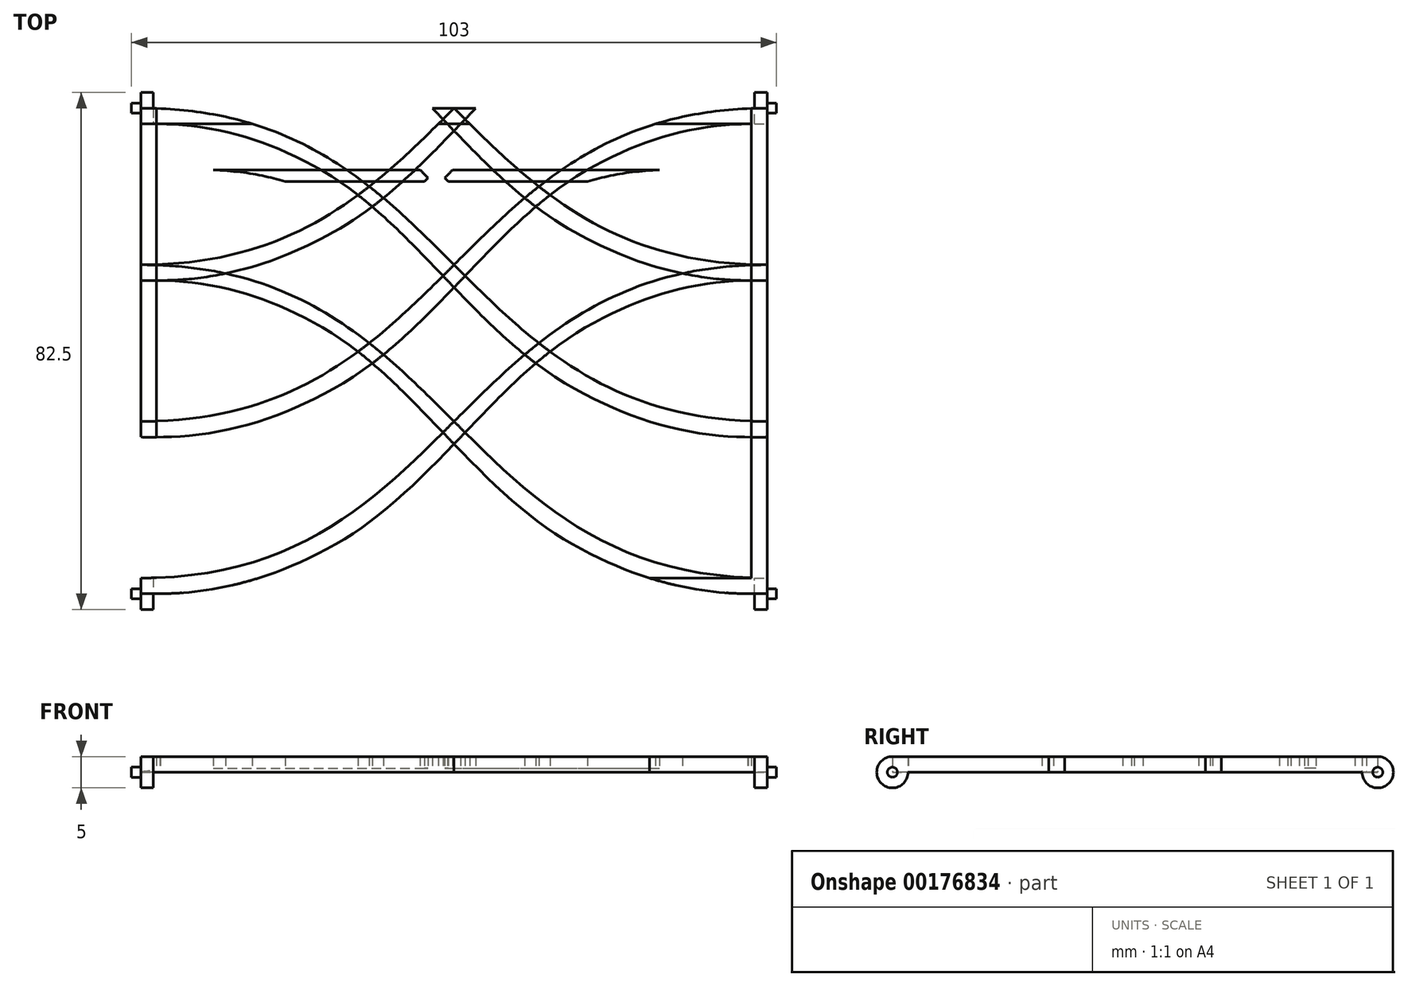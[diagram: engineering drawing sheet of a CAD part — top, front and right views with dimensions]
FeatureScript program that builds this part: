
annotation { "Feature Type Name" : "Feature", "Feature Type Description" : "" }
export const myFeature = defineFeature(function(context is Context, id is Id, definition is map)
    precondition{}
    {
        {
            var Q0;
            Q0=qCreatedBy(makeId("Top.planeOp"),FACE);
            var sketch = newSketch(context, id + "F0", { "sketchPlane" : qUnion([Q0])});
            skLineSegment(sketch, "E0.bottom", {"start": v(-50, 50) * mm, "end": v(50, 50) * mm});
            skLineSegment(sketch, "E0.top", {"start": v(-50, -50) * mm, "end": v(50, -50) * mm});
            skLineSegment(sketch, "E0.left", {"start": v(-50, 50) * mm, "end": v(-50, -50) * mm});
            skLineSegment(sketch, "E0.right", {"start": v(50, 50) * mm, "end": v(50, -50) * mm});
            skPoint(sketch, "E0.middle", {"position": v(0, 0) * mm});
            skLineSegment(sketch, "E1", {"start": v(-50, 50) * mm, "end": v(-50, 25) * mm});
            skLineSegment(sketch, "E2", {"start": v(-50, 25) * mm, "end": v(-50, 0) * mm});
            skLineSegment(sketch, "E3", {"start": v(-50, 0) * mm, "end": v(-50, -25) * mm});
            skLineSegment(sketch, "E4", {"start": v(-50, -25) * mm, "end": v(-50, -50) * mm});
            skFitSpline(sketch, "E5", {"points": [v(-50, 50) * mm, v(50, 0) * mm], "startDerivative": vector(150, 0) * mm, "endDerivative": vector(150, 0) * mm});
            skFitSpline(sketch, "E6", {"points": [v(-50, 25) * mm, v(50, -25) * mm], "startDerivative": vector(150, 0) * mm, "endDerivative": vector(150, 0) * mm});
            skFitSpline(sketch, "E7", {"points": [v(-50, 0) * mm, v(50, -50) * mm], "startDerivative": vector(150, 0) * mm, "endDerivative": vector(150, 0) * mm});
            skFitSpline(sketch, "E8", {"points": [v(-50, -50) * mm, v(50, 0) * mm], "startDerivative": vector(150, 0) * mm, "endDerivative": vector(150, 0) * mm});
            skFitSpline(sketch, "E9", {"points": [v(-50, -25) * mm, v(50, 25) * mm], "startDerivative": vector(150, 0) * mm, "endDerivative": vector(150, 0) * mm});
            skFitSpline(sketch, "E10", {"points": [v(-50, 0) * mm, v(50, 50) * mm], "startDerivative": vector(150, 0) * mm, "endDerivative": vector(150, 0) * mm});
            skFitSpline(sketch, "E11.0", {"points": [v(-50, 47.5) * mm, v(-46.98, 47.5) * mm, v(-41.34, 47.12) * mm, v(-33.93, 45.58) * mm, v(-27.38, 43.21) * mm, v(-19.56, 39.12) * mm, v(-11.07, 32.53) * mm, v(-1.8, 23.27) * mm, v(7.68, 13.78) * mm, v(16.77, 6.7) * mm, v(25.36, 2.2) * mm, v(32.58, -0.41) * mm, v(40.69, -2.1) * mm, v(46.77, -2.5) * mm, v(50, -2.5) * mm]});
            skFitSpline(sketch, "E12.0", {"points": [v(-50, -2.5) * mm, v(-46.77, -2.5) * mm, v(-40.69, -2.1) * mm, v(-32.58, -0.41) * mm, v(-25.36, 2.2) * mm, v(-16.77, 6.7) * mm, v(-7.68, 13.78) * mm, v(1.8, 23.27) * mm, v(11.07, 32.53) * mm, v(19.56, 39.12) * mm, v(27.38, 43.21) * mm, v(33.93, 45.58) * mm, v(41.34, 47.12) * mm, v(46.98, 47.5) * mm, v(50, 47.5) * mm]});
            skFitSpline(sketch, "E13.0", {"points": [v(-50, 22.5) * mm, v(-46.98, 22.5) * mm, v(-41.34, 22.12) * mm, v(-33.93, 20.58) * mm, v(-27.38, 18.21) * mm, v(-19.56, 14.12) * mm, v(-11.07, 7.53) * mm, v(-1.8, -1.73) * mm, v(7.68, -11.22) * mm, v(16.77, -18.3) * mm, v(25.36, -22.8) * mm, v(32.58, -25.41) * mm, v(40.69, -27.1) * mm, v(46.77, -27.5) * mm, v(50, -27.5) * mm]});
            skFitSpline(sketch, "E14.0", {"points": [v(-50, -27.5) * mm, v(-46.77, -27.5) * mm, v(-40.69, -27.1) * mm, v(-32.58, -25.41) * mm, v(-25.36, -22.8) * mm, v(-16.77, -18.3) * mm, v(-7.68, -11.22) * mm, v(1.8, -1.73) * mm, v(11.07, 7.53) * mm, v(19.56, 14.12) * mm, v(27.38, 18.21) * mm, v(33.93, 20.58) * mm, v(41.34, 22.12) * mm, v(46.98, 22.5) * mm, v(50, 22.5) * mm]});
            skFitSpline(sketch, "E15.0", {"points": [v(-50, -2.5) * mm, v(-46.98, -2.5) * mm, v(-41.34, -2.88) * mm, v(-33.93, -4.42) * mm, v(-27.38, -6.79) * mm, v(-19.56, -10.88) * mm, v(-11.07, -17.47) * mm, v(-1.8, -26.73) * mm, v(7.68, -36.22) * mm, v(16.77, -43.3) * mm, v(25.36, -47.8) * mm, v(32.58, -50.41) * mm, v(40.69, -52.1) * mm, v(46.77, -52.5) * mm, v(50, -52.5) * mm]});
            skFitSpline(sketch, "E16.0", {"points": [v(-50, -52.5) * mm, v(-46.77, -52.5) * mm, v(-40.69, -52.1) * mm, v(-32.58, -50.41) * mm, v(-25.36, -47.8) * mm, v(-16.77, -43.3) * mm, v(-7.68, -36.22) * mm, v(1.8, -26.73) * mm, v(11.07, -17.47) * mm, v(19.56, -10.88) * mm, v(27.38, -6.79) * mm, v(33.93, -4.42) * mm, v(41.34, -2.88) * mm, v(46.98, -2.5) * mm, v(50, -2.5) * mm]});
            skLineSegment(sketch, "E17", {"start": v(-50, -50) * mm, "end": v(-50, -52.5) * mm});
            skLineSegment(sketch, "E18", {"start": v(50, -52.5) * mm, "end": v(50, -50) * mm});
            skLineSegment(sketch, "E19", {"start": v(-50, 25) * mm, "end": v(50, 25) * mm});
            skLineSegment(sketch, "E20", {"start": v(-50, 25) * mm, "end": v(-47.5, 25) * mm});
            skLineSegment(sketch, "E21", {"start": v(50, 25) * mm, "end": v(47.5, 25) * mm});
            skLineSegment(sketch, "E22", {"start": v(-50, 22.5) * mm, "end": v(50, 22.5) * mm});
            skLineSegment(sketch, "E23", {"start": v(-47.5, 25) * mm, "end": v(-47.5, -49.96) * mm});
            skLineSegment(sketch, "E24", {"start": v(47.5, 25) * mm, "end": v(47.5, -50) * mm});
            skSolve(sketch);
        }
        {
            var Q0;
            {var subQ0=sQuery(id+"F0.wireOp",EDGE,"E23");var subQ9=sQuery(id+"F0.wireOp",EDGE,"E6");var subQ10=makeQuery(id+"F0.imprint","INTERSECT",VERTEX,{"derivedFrom":[subQ9,subQ0]});Q0=makeQuery(id+"F0.imprint","IMPRINT",FACE,{"disambiguationData":[TD([[makeQuery(id+"F0.imprint","IMPRINT",EDGE,{"disambiguationData":[TD([[subQ10,-1.0]])],"derivedFrom":subQ9}),1.0]])]});}
            var Q1;
            {var subQ0=sQuery(id+"F0.wireOp",EDGE,"E8");var subQ1=sQuery(id+"F0.wireOp",EDGE,"E7");var subQ2=makeQuery(id+"F0.imprint","INTERSECT",VERTEX,{"derivedFrom":[subQ1,subQ0]});Q1=makeQuery(id+"F0.imprint","IMPRINT",FACE,{"disambiguationData":[TD([[makeQuery(id+"F0.imprint","IMPRINT",EDGE,{"disambiguationData":[TD([[subQ2,-1.0]])],"derivedFrom":subQ1}),1.0]])]});}
            var Q2;
            {var subQ0=sQuery(id+"F0.wireOp",EDGE,"E16.0");var subQ1=sQuery(id+"F0.wireOp",EDGE,"E6");var subQ2=makeQuery(id+"F0.imprint","INTERSECT",VERTEX,{"derivedFrom":[subQ1,subQ0]});Q2=makeQuery(id+"F0.imprint","IMPRINT",FACE,{"disambiguationData":[TD([[makeQuery(id+"F0.imprint","IMPRINT",EDGE,{"disambiguationData":[TD([[subQ2,-1.0]])],"derivedFrom":subQ1}),-1.0]])]});}
            var Q3;
            {var subQ0=sQuery(id+"F0.wireOp",EDGE,"E9");var subQ1=sQuery(id+"F0.wireOp",EDGE,"E5");var subQ2=makeQuery(id+"F0.imprint","INTERSECT",VERTEX,{"derivedFrom":[subQ1,subQ0]});Q3=makeQuery(id+"F0.imprint","IMPRINT",FACE,{"disambiguationData":[TD([[makeQuery(id+"F0.imprint","IMPRINT",EDGE,{"disambiguationData":[TD([[subQ2,-1.0]])],"derivedFrom":subQ1}),-1.0]])]});}
            var Q4;
            {var subQ0=sQuery(id+"F0.wireOp",EDGE,"E9");var subQ1=sQuery(id+"F0.wireOp",EDGE,"E6");var subQ2=makeQuery(id+"F0.imprint","INTERSECT",VERTEX,{"derivedFrom":[subQ1,subQ0]});Q4=makeQuery(id+"F0.imprint","IMPRINT",FACE,{"disambiguationData":[TD([[makeQuery(id+"F0.imprint","IMPRINT",EDGE,{"disambiguationData":[TD([[subQ2,-1.0]])],"derivedFrom":subQ1}),1.0]])]});}
            var Q5;
            {var subQ1=sQuery(id+"F0.wireOp",EDGE,"E0.top");var subQ7=sQuery(id+"F0.wireOp",EDGE,"E24");var subQ9=makeQuery(id+"F0.imprint","INTERSECT",VERTEX,{"derivedFrom":[subQ1,subQ7]});Q5=makeQuery(id+"F0.imprint","IMPRINT",FACE,{"disambiguationData":[TD([[makeQuery(id+"F0.imprint","IMPRINT",EDGE,{"disambiguationData":[TD([[subQ9,1.0]])],"derivedFrom":subQ1}),1.0]])]});}
            var Q6;
            {var subQ0=sQuery(id+"F0.wireOp",EDGE,"E12.0");var subQ1=sQuery(id+"F0.wireOp",EDGE,"E6");var subQ2=makeQuery(id+"F0.imprint","INTERSECT",VERTEX,{"derivedFrom":[subQ1,subQ0]});Q6=makeQuery(id+"F0.imprint","IMPRINT",FACE,{"disambiguationData":[TD([[makeQuery(id+"F0.imprint","IMPRINT",EDGE,{"disambiguationData":[TD([[subQ2,-1.0]])],"derivedFrom":subQ1}),-1.0]])]});}
            var Q7;
            {var subQ0=sQuery(id+"F0.wireOp",EDGE,"E22");var subQ1=sQuery(id+"F0.wireOp",EDGE,"E6");var subQ2=makeQuery(id+"F0.imprint","INTERSECT",VERTEX,{"derivedFrom":[subQ1,subQ0]});Q7=makeQuery(id+"F0.imprint","IMPRINT",FACE,{"disambiguationData":[TD([[makeQuery(id+"F0.imprint","IMPRINT",EDGE,{"disambiguationData":[TD([[subQ2,-1.0]])],"derivedFrom":subQ1}),-1.0]])]});}
            var Q8;
            {var subQ0=sQuery(id+"F0.wireOp",EDGE,"E9");var subQ1=sQuery(id+"F0.wireOp",EDGE,"E7");var subQ2=makeQuery(id+"F0.imprint","INTERSECT",VERTEX,{"derivedFrom":[subQ1,subQ0]});Q8=makeQuery(id+"F0.imprint","IMPRINT",FACE,{"disambiguationData":[TD([[makeQuery(id+"F0.imprint","IMPRINT",EDGE,{"disambiguationData":[TD([[subQ2,-1.0]])],"derivedFrom":subQ1}),-1.0]])]});}
            var Q9;
            {var subQ1=sQuery(id+"F0.wireOp",EDGE,"E0.right");var subQ3=sQuery(id+"F0.wireOp",EDGE,"E13.0");var subQ4=makeQuery(id+"F0.imprint","INTERSECT",VERTEX,{"derivedFrom":[subQ1,subQ3]});Q9=makeQuery(id+"F0.imprint","IMPRINT",FACE,{"disambiguationData":[TD([[makeQuery(id+"F0.imprint","IMPRINT",EDGE,{"disambiguationData":[TD([[subQ4,1.0]])],"derivedFrom":subQ3}),-1.0]])]});}
            var Q10;
            {var subQ1=sQuery(id+"F0.wireOp",EDGE,"E8");var subQ5=makeQuery(id+"F0.imprint","INTERSECT",VERTEX,{"derivedFrom":[subQ1,sQuery(id+"F0.wireOp",EDGE,"E23")]});Q10=makeQuery(id+"F0.imprint","IMPRINT",FACE,{"disambiguationData":[TD([[makeQuery(id+"F0.imprint","IMPRINT",EDGE,{"disambiguationData":[TD([[subQ5,-1.0]])],"derivedFrom":subQ1}),-1.0]])]});}
            var Q11;
            {var subQ0=sQuery(id+"F0.wireOp",EDGE,"E6");var subQ1=sQuery(id+"F0.wireOp",EDGE,"E0.right");var subQ2=makeQuery(id+"F0.imprint","INTERSECT",VERTEX,{"derivedFrom":[subQ1,subQ0]});Q11=makeQuery(id+"F0.imprint","IMPRINT",FACE,{"disambiguationData":[TD([[makeQuery(id+"F0.imprint","IMPRINT",EDGE,{"disambiguationData":[TD([[subQ2,1.0]])],"derivedFrom":subQ0}),1.0]])]});}
            var Q12;
            {var subQ0=sQuery(id+"F0.wireOp",EDGE,"E5");var subQ5=sQuery(id+"F0.wireOp",EDGE,"E24");var subQ6=makeQuery(id+"F0.imprint","INTERSECT",VERTEX,{"derivedFrom":[subQ0,subQ5]});Q12=makeQuery(id+"F0.imprint","IMPRINT",FACE,{"disambiguationData":[TD([[makeQuery(id+"F0.imprint","IMPRINT",EDGE,{"disambiguationData":[TD([[subQ6,1.0]])],"derivedFrom":subQ5}),1.0]])]});}
            var Q13;
            {var subQ3=sQuery(id+"F0.wireOp",EDGE,"E12.0");var subQ5=sQuery(id+"F0.wireOp",EDGE,"E5");var subQ6=makeQuery(id+"F0.imprint","INTERSECT",VERTEX,{"derivedFrom":[subQ5,subQ3]});Q13=makeQuery(id+"F0.imprint","IMPRINT",FACE,{"disambiguationData":[TD([[makeQuery(id+"F0.imprint","IMPRINT",EDGE,{"disambiguationData":[TD([[subQ6,-1.0]])],"derivedFrom":subQ5}),1.0]])]});}
            var Q14;
            {var subQ1=sQuery(id+"F0.wireOp",EDGE,"E6");var subQ7=sQuery(id+"F0.wireOp",EDGE,"E10");var subQ8=makeQuery(id+"F0.imprint","INTERSECT",VERTEX,{"derivedFrom":[subQ1,subQ7]});Q14=makeQuery(id+"F0.imprint","IMPRINT",FACE,{"disambiguationData":[TD([[makeQuery(id+"F0.imprint","IMPRINT",EDGE,{"disambiguationData":[TD([[subQ8,-1.0]])],"derivedFrom":subQ1}),1.0]])]});}
            var Q15;
            {var subQ0=sQuery(id+"F0.wireOp",EDGE,"E10");var subQ5=sQuery(id+"F0.wireOp",EDGE,"E23");var subQ6=makeQuery(id+"F0.imprint","INTERSECT",VERTEX,{"derivedFrom":[subQ0,subQ5]});Q15=makeQuery(id+"F0.imprint","IMPRINT",FACE,{"disambiguationData":[TD([[makeQuery(id+"F0.imprint","IMPRINT",EDGE,{"disambiguationData":[TD([[subQ6,1.0]])],"derivedFrom":subQ5}),-1.0]])]});}
            var Q16;
            {var subQ0=sQuery(id+"F0.wireOp",EDGE,"E14.0");var subQ1=sQuery(id+"F0.wireOp",EDGE,"E5");var subQ2=makeQuery(id+"F0.imprint","INTERSECT",VERTEX,{"derivedFrom":[subQ1,subQ0]});Q16=makeQuery(id+"F0.imprint","IMPRINT",FACE,{"disambiguationData":[TD([[makeQuery(id+"F0.imprint","IMPRINT",EDGE,{"disambiguationData":[TD([[subQ2,-1.0]])],"derivedFrom":subQ1}),-1.0]])]});}
            var Q17;
            {var subQ4=sQuery(id+"F0.wireOp",EDGE,"E18");Q17=makeQuery(id+"F0.imprint","IMPRINT",FACE,{"disambiguationData":[TD([[makeQuery(id+"F0.imprint","IMPRINT",EDGE,{"derivedFrom":subQ4}),1.0]])]});}
            var Q18;
            {var subQ0=sQuery(id+"F0.wireOp",EDGE,"E23");var subQ1=sQuery(id+"F0.wireOp",EDGE,"E6");var subQ2=makeQuery(id+"F0.imprint","INTERSECT",VERTEX,{"derivedFrom":[subQ1,subQ0]});Q18=makeQuery(id+"F0.imprint","IMPRINT",FACE,{"disambiguationData":[TD([[makeQuery(id+"F0.imprint","IMPRINT",EDGE,{"disambiguationData":[TD([[subQ2,-1.0]])],"derivedFrom":subQ1}),-1.0]])]});}
            var Q19;
            {var subQ0=sQuery(id+"F0.wireOp",EDGE,"E8");var subQ1=sQuery(id+"F0.wireOp",EDGE,"E6");var subQ2=makeQuery(id+"F0.imprint","INTERSECT",VERTEX,{"derivedFrom":[subQ1,subQ0]});Q19=makeQuery(id+"F0.imprint","IMPRINT",FACE,{"disambiguationData":[TD([[makeQuery(id+"F0.imprint","IMPRINT",EDGE,{"disambiguationData":[TD([[subQ2,-1.0]])],"derivedFrom":subQ1}),-1.0]])]});}
            var Q20;
            {var subQ0=sQuery(id+"F0.wireOp",EDGE,"E17");Q20=makeQuery(id+"F0.imprint","IMPRINT",FACE,{"disambiguationData":[TD([[makeQuery(id+"F0.imprint","IMPRINT",EDGE,{"derivedFrom":subQ0}),1.0]])]});}
            var Q21;
            {var subQ0=sQuery(id+"F0.wireOp",EDGE,"E11.0");var subQ1=sQuery(id+"F0.wireOp",EDGE,"E8");var subQ2=makeQuery(id+"F0.imprint","INTERSECT",VERTEX,{"derivedFrom":[subQ1,subQ0]});Q21=makeQuery(id+"F0.imprint","IMPRINT",FACE,{"disambiguationData":[TD([[makeQuery(id+"F0.imprint","IMPRINT",EDGE,{"disambiguationData":[TD([[subQ2,-1.0]])],"derivedFrom":subQ1}),-1.0]])]});}
            var Q22;
            {var subQ0=sQuery(id+"F0.wireOp",EDGE,"E10");var subQ1=sQuery(id+"F0.wireOp",EDGE,"E6");var subQ2=makeQuery(id+"F0.imprint","INTERSECT",VERTEX,{"derivedFrom":[subQ1,subQ0]});Q22=makeQuery(id+"F0.imprint","IMPRINT",FACE,{"disambiguationData":[TD([[makeQuery(id+"F0.imprint","IMPRINT",EDGE,{"disambiguationData":[TD([[subQ2,-1.0]])],"derivedFrom":subQ1}),-1.0]])]});}
            var Q23;
            {var subQ1=sQuery(id+"F0.wireOp",EDGE,"E5");var subQ5=sQuery(id+"F0.wireOp",EDGE,"E9");var subQ6=makeQuery(id+"F0.imprint","INTERSECT",VERTEX,{"derivedFrom":[subQ1,subQ5]});Q23=makeQuery(id+"F0.imprint","IMPRINT",FACE,{"disambiguationData":[TD([[makeQuery(id+"F0.imprint","IMPRINT",EDGE,{"disambiguationData":[TD([[subQ6,-1.0]])],"derivedFrom":subQ1}),1.0]])]});}
            var Q24;
            {var subQ0=sQuery(id+"F0.wireOp",EDGE,"E9");var subQ1=sQuery(id+"F0.wireOp",EDGE,"E7");var subQ2=makeQuery(id+"F0.imprint","INTERSECT",VERTEX,{"derivedFrom":[subQ1,subQ0]});Q24=makeQuery(id+"F0.imprint","IMPRINT",FACE,{"disambiguationData":[TD([[makeQuery(id+"F0.imprint","IMPRINT",EDGE,{"disambiguationData":[TD([[subQ2,-1.0]])],"derivedFrom":subQ1}),1.0]])]});}
            var Q25;
            {var subQ1=sQuery(id+"F0.wireOp",EDGE,"E4");var subQ3=sQuery(id+"F0.wireOp",EDGE,"E14.0");var subQ4=makeQuery(id+"F0.imprint","INTERSECT",VERTEX,{"derivedFrom":[subQ1,subQ3]});Q25=makeQuery(id+"F0.imprint","IMPRINT",FACE,{"disambiguationData":[TD([[makeQuery(id+"F0.imprint","IMPRINT",EDGE,{"disambiguationData":[TD([[subQ4,-1.0]])],"derivedFrom":subQ3}),-1.0]])]});}
            var Q26;
            {var subQ5=sQuery(id+"F0.wireOp",EDGE,"E12.0");var subQ6=sQuery(id+"F0.wireOp",EDGE,"E7");var subQ7=makeQuery(id+"F0.imprint","INTERSECT",VERTEX,{"derivedFrom":[subQ6,subQ5]});Q26=makeQuery(id+"F0.imprint","IMPRINT",FACE,{"disambiguationData":[TD([[makeQuery(id+"F0.imprint","IMPRINT",EDGE,{"disambiguationData":[TD([[subQ7,-1.0]])],"derivedFrom":subQ6}),-1.0]])]});}
            var Q27;
            {var subQ0=sQuery(id+"F0.wireOp",EDGE,"E9");var subQ5=sQuery(id+"F0.wireOp",EDGE,"E23");var subQ6=makeQuery(id+"F0.imprint","INTERSECT",VERTEX,{"derivedFrom":[subQ0,subQ5]});Q27=makeQuery(id+"F0.imprint","IMPRINT",FACE,{"disambiguationData":[TD([[makeQuery(id+"F0.imprint","IMPRINT",EDGE,{"disambiguationData":[TD([[subQ6,1.0]])],"derivedFrom":subQ5}),-1.0]])]});}
            var Q28;
            {var subQ1=sQuery(id+"F0.wireOp",EDGE,"E8");var subQ6=sQuery(id+"F0.wireOp",EDGE,"E6");var subQ9=makeQuery(id+"F0.imprint","INTERSECT",VERTEX,{"derivedFrom":[subQ6,subQ1]});Q28=makeQuery(id+"F0.imprint","IMPRINT",FACE,{"disambiguationData":[TD([[makeQuery(id+"F0.imprint","IMPRINT",EDGE,{"disambiguationData":[TD([[subQ9,-1.0]])],"derivedFrom":subQ6}),1.0]])]});}
            var Q29;
            {var subQ0=sQuery(id+"F0.wireOp",EDGE,"E22");var subQ1=sQuery(id+"F0.wireOp",EDGE,"E9");var subQ2=makeQuery(id+"F0.imprint","INTERSECT",VERTEX,{"derivedFrom":[subQ1,subQ0]});Q29=makeQuery(id+"F0.imprint","IMPRINT",FACE,{"disambiguationData":[TD([[makeQuery(id+"F0.imprint","IMPRINT",EDGE,{"disambiguationData":[TD([[subQ2,-1.0]])],"derivedFrom":subQ1}),-1.0]])]});}
            var Q30;
            {var subQ0=sQuery(id+"F0.wireOp",EDGE,"E14.0");var subQ1=sQuery(id+"F0.wireOp",EDGE,"E6");var subQ2=makeQuery(id+"F0.imprint","INTERSECT",VERTEX,{"derivedFrom":[subQ1,subQ0]});Q30=makeQuery(id+"F0.imprint","IMPRINT",FACE,{"disambiguationData":[TD([[makeQuery(id+"F0.imprint","IMPRINT",EDGE,{"disambiguationData":[TD([[subQ2,-1.0]])],"derivedFrom":subQ1}),-1.0]])]});}
            var Q31;
            {var subQ3=sQuery(id+"F0.wireOp",EDGE,"E22");var subQ6=sQuery(id+"F0.wireOp",EDGE,"E5");var subQ9=makeQuery(id+"F0.imprint","INTERSECT",VERTEX,{"derivedFrom":[subQ6,subQ3]});Q31=makeQuery(id+"F0.imprint","IMPRINT",FACE,{"disambiguationData":[TD([[makeQuery(id+"F0.imprint","IMPRINT",EDGE,{"disambiguationData":[TD([[subQ9,-1.0]])],"derivedFrom":subQ6}),-1.0]])]});}
            var Q32;
            {var subQ0=sQuery(id+"F0.wireOp",EDGE,"E14.0");var subQ1=sQuery(id+"F0.wireOp",EDGE,"E7");var subQ2=makeQuery(id+"F0.imprint","INTERSECT",VERTEX,{"derivedFrom":[subQ1,subQ0]});Q32=makeQuery(id+"F0.imprint","IMPRINT",FACE,{"disambiguationData":[TD([[makeQuery(id+"F0.imprint","IMPRINT",EDGE,{"disambiguationData":[TD([[subQ2,-1.0]])],"derivedFrom":subQ1}),-1.0]])]});}
            var Q33;
            {var subQ0=sQuery(id+"F0.wireOp",EDGE,"E23");var subQ1=sQuery(id+"F0.wireOp",EDGE,"E7");var subQ2=makeQuery(id+"F0.imprint","INTERSECT",VERTEX,{"derivedFrom":[subQ1,subQ0]});Q33=makeQuery(id+"F0.imprint","IMPRINT",FACE,{"disambiguationData":[TD([[makeQuery(id+"F0.imprint","IMPRINT",EDGE,{"disambiguationData":[TD([[subQ2,-1.0]])],"derivedFrom":subQ1}),-1.0]])]});}
            var Q34;
            {var subQ0=sQuery(id+"F0.wireOp",EDGE,"E23");var subQ1=sQuery(id+"F0.wireOp",EDGE,"E9");var subQ2=makeQuery(id+"F0.imprint","INTERSECT",VERTEX,{"derivedFrom":[subQ1,subQ0]});Q34=makeQuery(id+"F0.imprint","IMPRINT",FACE,{"disambiguationData":[TD([[makeQuery(id+"F0.imprint","IMPRINT",EDGE,{"disambiguationData":[TD([[subQ2,-1.0]])],"derivedFrom":subQ1}),-1.0]])]});}
            var Q35;
            {var subQ5=sQuery(id+"F0.wireOp",EDGE,"E23");var subQ6=sQuery(id+"F0.wireOp",EDGE,"E7");var subQ7=makeQuery(id+"F0.imprint","INTERSECT",VERTEX,{"derivedFrom":[subQ6,subQ5]});Q35=makeQuery(id+"F0.imprint","IMPRINT",FACE,{"disambiguationData":[TD([[makeQuery(id+"F0.imprint","IMPRINT",EDGE,{"disambiguationData":[TD([[subQ7,-1.0]])],"derivedFrom":subQ6}),1.0]])]});}
            var Q36;
            {var subQ0=sQuery(id+"F0.wireOp",EDGE,"E12.0");var subQ1=sQuery(id+"F0.wireOp",EDGE,"E5");var subQ2=makeQuery(id+"F0.imprint","INTERSECT",VERTEX,{"derivedFrom":[subQ1,subQ0]});Q36=makeQuery(id+"F0.imprint","IMPRINT",FACE,{"disambiguationData":[TD([[makeQuery(id+"F0.imprint","IMPRINT",EDGE,{"disambiguationData":[TD([[subQ2,-1.0]])],"derivedFrom":subQ1}),-1.0]])]});}
            var Q37;
            {var subQ1=sQuery(id+"F0.wireOp",EDGE,"E7");var subQ3=sQuery(id+"F0.wireOp",EDGE,"E23");var subQ4=makeQuery(id+"F0.imprint","INTERSECT",VERTEX,{"derivedFrom":[subQ1,subQ3]});Q37=makeQuery(id+"F0.imprint","IMPRINT",FACE,{"disambiguationData":[TD([[makeQuery(id+"F0.imprint","IMPRINT",EDGE,{"disambiguationData":[TD([[subQ4,1.0]])],"derivedFrom":subQ3}),-1.0]])]});}
            var Q38;
            {var subQ0=sQuery(id+"F0.wireOp",EDGE,"E22");var subQ1=sQuery(id+"F0.wireOp",EDGE,"E10");var subQ2=makeQuery(id+"F0.imprint","INTERSECT",VERTEX,{"derivedFrom":[subQ1,subQ0]});Q38=makeQuery(id+"F0.imprint","IMPRINT",FACE,{"disambiguationData":[TD([[makeQuery(id+"F0.imprint","IMPRINT",EDGE,{"disambiguationData":[TD([[subQ2,-1.0]])],"derivedFrom":subQ1}),-1.0]])]});}
            var Q39;
            {var subQ0=sQuery(id+"F0.wireOp",EDGE,"E7");var subQ5=sQuery(id+"F0.wireOp",EDGE,"E23");var subQ6=makeQuery(id+"F0.imprint","INTERSECT",VERTEX,{"derivedFrom":[subQ0,subQ5]});Q39=makeQuery(id+"F0.imprint","IMPRINT",FACE,{"disambiguationData":[TD([[makeQuery(id+"F0.imprint","IMPRINT",EDGE,{"disambiguationData":[TD([[subQ6,-1.0]])],"derivedFrom":subQ5}),-1.0]])]});}
            var Q40;
            {var subQ0=sQuery(id+"F0.wireOp",EDGE,"E8");var subQ5=sQuery(id+"F0.wireOp",EDGE,"E24");var subQ6=makeQuery(id+"F0.imprint","INTERSECT",VERTEX,{"derivedFrom":[subQ0,subQ5]});Q40=makeQuery(id+"F0.imprint","IMPRINT",FACE,{"disambiguationData":[TD([[makeQuery(id+"F0.imprint","IMPRINT",EDGE,{"disambiguationData":[TD([[subQ6,-1.0]])],"derivedFrom":subQ5}),1.0]])]});}
            var Q41;
            {var subQ0=sQuery(id+"F0.wireOp",EDGE,"E6");var subQ1=sQuery(id+"F0.wireOp",EDGE,"E0.right");var subQ2=makeQuery(id+"F0.imprint","INTERSECT",VERTEX,{"derivedFrom":[subQ1,subQ0]});Q41=makeQuery(id+"F0.imprint","IMPRINT",FACE,{"disambiguationData":[TD([[makeQuery(id+"F0.imprint","IMPRINT",EDGE,{"disambiguationData":[TD([[subQ2,-1.0]])],"derivedFrom":subQ1}),-1.0]])]});}
            var Q42;
            {var subQ0=sQuery(id+"F0.wireOp",EDGE,"E22");var subQ1=sQuery(id+"F0.wireOp",EDGE,"E11.0");var subQ2=makeQuery(id+"F0.imprint","INTERSECT",VERTEX,{"derivedFrom":[subQ1,subQ0]});Q42=makeQuery(id+"F0.imprint","IMPRINT",FACE,{"disambiguationData":[TD([[makeQuery(id+"F0.imprint","IMPRINT",EDGE,{"disambiguationData":[TD([[subQ2,-1.0]])],"derivedFrom":subQ1}),1.0]])]});}
            var Q43;
            {var subQ1=sQuery(id+"F0.wireOp",EDGE,"E0.top");var subQ3=sQuery(id+"F0.wireOp",EDGE,"E24");var subQ4=makeQuery(id+"F0.imprint","INTERSECT",VERTEX,{"derivedFrom":[subQ1,subQ3]});Q43=makeQuery(id+"F0.imprint","IMPRINT",FACE,{"disambiguationData":[TD([[makeQuery(id+"F0.imprint","IMPRINT",EDGE,{"disambiguationData":[TD([[subQ4,1.0]])],"derivedFrom":subQ3}),1.0]])]});}
            var Q44;
            {var subQ1=sQuery(id+"F0.wireOp",EDGE,"E14.0");var subQ3=sQuery(id+"F0.wireOp",EDGE,"E24");var subQ4=makeQuery(id+"F0.imprint","INTERSECT",VERTEX,{"derivedFrom":[subQ1,subQ3]});Q44=makeQuery(id+"F0.imprint","IMPRINT",FACE,{"disambiguationData":[TD([[makeQuery(id+"F0.imprint","IMPRINT",EDGE,{"disambiguationData":[TD([[subQ4,1.0]])],"derivedFrom":subQ3}),1.0]])]});}
            var Q45;
            {var subQ0=sQuery(id+"F0.wireOp",EDGE,"E8");var subQ1=sQuery(id+"F0.wireOp",EDGE,"E7");var subQ2=makeQuery(id+"F0.imprint","INTERSECT",VERTEX,{"derivedFrom":[subQ1,subQ0]});Q45=makeQuery(id+"F0.imprint","IMPRINT",FACE,{"disambiguationData":[TD([[makeQuery(id+"F0.imprint","IMPRINT",EDGE,{"disambiguationData":[TD([[subQ2,-1.0]])],"derivedFrom":subQ1}),-1.0]])]});}
            var Q46;
            {var subQ0=sQuery(id+"F0.wireOp",EDGE,"E9");var subQ1=sQuery(id+"F0.wireOp",EDGE,"E6");var subQ2=makeQuery(id+"F0.imprint","INTERSECT",VERTEX,{"derivedFrom":[subQ1,subQ0]});Q46=makeQuery(id+"F0.imprint","IMPRINT",FACE,{"disambiguationData":[TD([[makeQuery(id+"F0.imprint","IMPRINT",EDGE,{"disambiguationData":[TD([[subQ2,-1.0]])],"derivedFrom":subQ1}),-1.0]])]});}
            var Q47;
            {var subQ1=sQuery(id+"F0.wireOp",EDGE,"E11.0");var subQ3=sQuery(id+"F0.wireOp",EDGE,"E24");var subQ4=makeQuery(id+"F0.imprint","INTERSECT",VERTEX,{"derivedFrom":[subQ1,subQ3]});Q47=makeQuery(id+"F0.imprint","IMPRINT",FACE,{"disambiguationData":[TD([[makeQuery(id+"F0.imprint","IMPRINT",EDGE,{"disambiguationData":[TD([[subQ4,-1.0]])],"derivedFrom":subQ3}),1.0]])]});}
            var Q48;
            {var subQ0=sQuery(id+"F0.wireOp",EDGE,"E11.0");var subQ1=sQuery(id+"F0.wireOp",EDGE,"E10");var subQ2=makeQuery(id+"F0.imprint","INTERSECT",VERTEX,{"derivedFrom":[subQ1,subQ0]});Q48=makeQuery(id+"F0.imprint","IMPRINT",FACE,{"disambiguationData":[TD([[makeQuery(id+"F0.imprint","IMPRINT",EDGE,{"disambiguationData":[TD([[subQ2,-1.0]])],"derivedFrom":subQ0}),1.0]])]});}
            var Q49;
            {var subQ1=sQuery(id+"F0.wireOp",EDGE,"E13.0");var subQ3=sQuery(id+"F0.wireOp",EDGE,"E23");var subQ4=makeQuery(id+"F0.imprint","INTERSECT",VERTEX,{"derivedFrom":[subQ1,subQ3]});Q49=makeQuery(id+"F0.imprint","IMPRINT",FACE,{"disambiguationData":[TD([[makeQuery(id+"F0.imprint","IMPRINT",EDGE,{"disambiguationData":[TD([[subQ4,1.0]])],"derivedFrom":subQ3}),-1.0]])]});}
            var Q50;
            {var subQ1=sQuery(id+"F0.wireOp",EDGE,"E4");var subQ3=sQuery(id+"F0.wireOp",EDGE,"E14.0");var subQ4=makeQuery(id+"F0.imprint","INTERSECT",VERTEX,{"derivedFrom":[subQ1,subQ3]});Q50=makeQuery(id+"F0.imprint","IMPRINT",FACE,{"disambiguationData":[TD([[makeQuery(id+"F0.imprint","IMPRINT",EDGE,{"disambiguationData":[TD([[subQ4,-1.0]])],"derivedFrom":subQ3}),1.0]])]});}
            var Q51;
            {var subQ1=sQuery(id+"F0.wireOp",EDGE,"E5");var subQ3=sQuery(id+"F0.wireOp",EDGE,"E24");var subQ4=makeQuery(id+"F0.imprint","INTERSECT",VERTEX,{"derivedFrom":[subQ1,subQ3]});Q51=makeQuery(id+"F0.imprint","IMPRINT",FACE,{"disambiguationData":[TD([[makeQuery(id+"F0.imprint","IMPRINT",EDGE,{"disambiguationData":[TD([[subQ4,-1.0]])],"derivedFrom":subQ3}),1.0]])]});}
            var Q52;
            {var subQ0=sQuery(id+"F0.wireOp",EDGE,"E11.0");var subQ1=sQuery(id+"F0.wireOp",EDGE,"E10");var subQ2=makeQuery(id+"F0.imprint","INTERSECT",VERTEX,{"derivedFrom":[subQ1,subQ0]});Q52=makeQuery(id+"F0.imprint","IMPRINT",FACE,{"disambiguationData":[TD([[makeQuery(id+"F0.imprint","IMPRINT",EDGE,{"disambiguationData":[TD([[subQ2,1.0]])],"derivedFrom":subQ0}),1.0]])]});}
            var Q53;
            {var subQ0=sQuery(id+"F0.wireOp",EDGE,"E6");var subQ5=sQuery(id+"F0.wireOp",EDGE,"E23");var subQ6=makeQuery(id+"F0.imprint","INTERSECT",VERTEX,{"derivedFrom":[subQ0,subQ5]});Q53=makeQuery(id+"F0.imprint","IMPRINT",FACE,{"disambiguationData":[TD([[makeQuery(id+"F0.imprint","IMPRINT",EDGE,{"disambiguationData":[TD([[subQ6,-1.0]])],"derivedFrom":subQ5}),-1.0]])]});}
            var Q54;
            {var subQ0=sQuery(id+"F0.wireOp",EDGE,"E9");var subQ5=sQuery(id+"F0.wireOp",EDGE,"E24");var subQ6=makeQuery(id+"F0.imprint","INTERSECT",VERTEX,{"derivedFrom":[subQ0,subQ5]});Q54=makeQuery(id+"F0.imprint","IMPRINT",FACE,{"disambiguationData":[TD([[makeQuery(id+"F0.imprint","IMPRINT",EDGE,{"disambiguationData":[TD([[subQ6,-1.0]])],"derivedFrom":subQ5}),1.0]])]});}
            var Q55;
            {var subQ0=sQuery(id+"F0.wireOp",EDGE,"E12.0");var subQ1=sQuery(id+"F0.wireOp",EDGE,"E5");var subQ2=makeQuery(id+"F0.imprint","INTERSECT",VERTEX,{"derivedFrom":[subQ1,subQ0]});Q55=makeQuery(id+"F0.imprint","IMPRINT",FACE,{"disambiguationData":[TD([[makeQuery(id+"F0.imprint","IMPRINT",EDGE,{"disambiguationData":[TD([[subQ2,-1.0]])],"derivedFrom":subQ0}),1.0]])]});}
            var Q56;
            {var subQ1=sQuery(id+"F0.wireOp",EDGE,"E12.0");var subQ3=sQuery(id+"F0.wireOp",EDGE,"E23");var subQ4=makeQuery(id+"F0.imprint","INTERSECT",VERTEX,{"derivedFrom":[subQ1,subQ3]});Q56=makeQuery(id+"F0.imprint","IMPRINT",FACE,{"disambiguationData":[TD([[makeQuery(id+"F0.imprint","IMPRINT",EDGE,{"disambiguationData":[TD([[subQ4,-1.0]])],"derivedFrom":subQ3}),-1.0]])]});}
            extrude(context, id + "F1", {"entities" : qUnion([Q0, Q1, Q2, Q3, Q4, Q5, Q6, Q7, Q8, Q9, Q10, Q11, Q12, Q13, Q14, Q15, Q16, Q17, Q18, Q19, Q20, Q21, Q22, Q23, Q24, Q25, Q26, Q27, Q28, Q29, Q30, Q31, Q32, Q33, Q34, Q35, Q36, Q37, Q38, Q39, Q40, Q41, Q42, Q43, Q44, Q45, Q46, Q47, Q48, Q49, Q50, Q51, Q52, Q53, Q54, Q55, Q56]), "depth" : 2.5 * mm});
        }
        {
            var Q0;
            Q0=makeQuery(id+"F1.opExtrude","SWEPT_FACE",FACE,{"disambiguationData":[OSD([sQuery(id+"F0.wireOp",EDGE,"E2"),sQuery(id+"F0.wireOp",EDGE,"E3"),sQuery(id+"F0.wireOp",EDGE,"E4"),sQuery(id+"F0.wireOp",EDGE,"E17")])]});
            var sketch = newSketch(context, id + "F2", { "sketchPlane" : qUnion([Q0])});
            skCircle(sketch, "E25", {"center": v(52.5, 0) * mm, "radius": 0.8 * mm});
            skCircle(sketch, "E26", {"center": v(-25, 0) * mm, "radius": 0.8 * mm});
            skCircle(sketch, "E27", {"center": v(-25, 0) * mm, "radius": 2.5 * mm});
            skCircle(sketch, "E28", {"center": v(52.5, 0) * mm, "radius": 2.5 * mm});
            skSolve(sketch);
        }
        {
            var Q0;
            {var subQ0=sQuery(id+"F2.wireOp",EDGE,"E26");var subQ1=sQuery(id+"F0.wireOp",EDGE,"E2");var subQ2=makeQuery(id+"F1.opExtrude","SWEPT_EDGE",EDGE,{"disambiguationData":[OSD([sQuery(id+"F0.wireOp",EDGE,"E1"),subQ1,sQuery(id+"F0.wireOp",EDGE,"E6"),sQuery(id+"F0.wireOp",EDGE,"E20")])]});var subQ3=makeQuery(id+"F2.imprint","INTERSECT",VERTEX,{"derivedFrom":[subQ2,subQ0]});Q0=makeQuery(id+"F2.imprint","IMPRINT",FACE,{"disambiguationData":[TD([[makeQuery(id+"F2.imprint","IMPRINT",EDGE,{"disambiguationData":[TD([[subQ3,1.0]])],"derivedFrom":subQ0}),1.0]])]});}
            var Q1;
            {var subQ0=sQuery(id+"F2.wireOp",EDGE,"E26");var subQ1=sQuery(id+"F0.wireOp",EDGE,"E2");var subQ2=makeQuery(id+"F1.opExtrude","SWEPT_EDGE",EDGE,{"disambiguationData":[OSD([sQuery(id+"F0.wireOp",EDGE,"E1"),subQ1,sQuery(id+"F0.wireOp",EDGE,"E6"),sQuery(id+"F0.wireOp",EDGE,"E20")])]});var subQ3=makeQuery(id+"F2.imprint","INTERSECT",VERTEX,{"derivedFrom":[subQ2,subQ0]});Q1=makeQuery(id+"F2.imprint","IMPRINT",FACE,{"disambiguationData":[TD([[makeQuery(id+"F2.imprint","IMPRINT",EDGE,{"disambiguationData":[TD([[subQ3,-1.0]])],"derivedFrom":subQ0}),1.0]])]});}
            var Q2;
            {var subQ0=sQuery(id+"F2.wireOp",EDGE,"E26");var subQ1=sQuery(id+"F0.wireOp",EDGE,"E2");var subQ2=makeQuery(id+"F1.opExtrude","SWEPT_EDGE",EDGE,{"disambiguationData":[OSD([sQuery(id+"F0.wireOp",EDGE,"E1"),subQ1,sQuery(id+"F0.wireOp",EDGE,"E6"),sQuery(id+"F0.wireOp",EDGE,"E20")])]});var subQ3=makeQuery(id+"F2.imprint","INTERSECT",VERTEX,{"derivedFrom":[subQ2,subQ0]});Q2=makeQuery(id+"F2.imprint","IMPRINT",FACE,{"disambiguationData":[TD([[makeQuery(id+"F2.imprint","IMPRINT",EDGE,{"disambiguationData":[TD([[subQ3,1.0]])],"derivedFrom":subQ0}),-1.0]])]});}
            var Q3;
            {var subQ0=sQuery(id+"F2.wireOp",EDGE,"E26");var subQ1=sQuery(id+"F0.wireOp",EDGE,"E2");var subQ2=makeQuery(id+"F1.opExtrude","SWEPT_EDGE",EDGE,{"disambiguationData":[OSD([sQuery(id+"F0.wireOp",EDGE,"E1"),subQ1,sQuery(id+"F0.wireOp",EDGE,"E6"),sQuery(id+"F0.wireOp",EDGE,"E20")])]});var subQ3=makeQuery(id+"F2.imprint","INTERSECT",VERTEX,{"derivedFrom":[subQ2,subQ0]});Q3=makeQuery(id+"F2.imprint","IMPRINT",FACE,{"disambiguationData":[TD([[makeQuery(id+"F2.imprint","IMPRINT",EDGE,{"disambiguationData":[TD([[subQ3,-1.0]])],"derivedFrom":subQ0}),-1.0]])]});}
            var Q4;
            {var subQ0=sQuery(id+"F2.wireOp",EDGE,"E25");var subQ1=sQuery(id+"F0.wireOp",EDGE,"E17");var subQ2=makeQuery(id+"F1.opExtrude","SWEPT_EDGE",EDGE,{"disambiguationData":[OSD([sQuery(id+"F0.wireOp",EDGE,"E16.0"),subQ1])]});var subQ3=makeQuery(id+"F2.imprint","INTERSECT",VERTEX,{"derivedFrom":[subQ2,subQ0]});Q4=makeQuery(id+"F2.imprint","IMPRINT",FACE,{"disambiguationData":[TD([[makeQuery(id+"F2.imprint","IMPRINT",EDGE,{"disambiguationData":[TD([[subQ3,-1.0]])],"derivedFrom":subQ0}),1.0]])]});}
            var Q5;
            {var subQ0=sQuery(id+"F2.wireOp",EDGE,"E25");var subQ1=sQuery(id+"F0.wireOp",EDGE,"E17");var subQ2=makeQuery(id+"F1.opExtrude","SWEPT_EDGE",EDGE,{"disambiguationData":[OSD([sQuery(id+"F0.wireOp",EDGE,"E16.0"),subQ1])]});var subQ3=makeQuery(id+"F2.imprint","INTERSECT",VERTEX,{"derivedFrom":[subQ2,subQ0]});Q5=makeQuery(id+"F2.imprint","IMPRINT",FACE,{"disambiguationData":[TD([[makeQuery(id+"F2.imprint","IMPRINT",EDGE,{"disambiguationData":[TD([[subQ3,1.0]])],"derivedFrom":subQ0}),1.0]])]});}
            var Q6;
            {var subQ0=sQuery(id+"F2.wireOp",EDGE,"E25");var subQ1=sQuery(id+"F0.wireOp",EDGE,"E17");var subQ2=makeQuery(id+"F1.opExtrude","SWEPT_EDGE",EDGE,{"disambiguationData":[OSD([sQuery(id+"F0.wireOp",EDGE,"E16.0"),subQ1])]});var subQ3=makeQuery(id+"F2.imprint","INTERSECT",VERTEX,{"derivedFrom":[subQ2,subQ0]});Q6=makeQuery(id+"F2.imprint","IMPRINT",FACE,{"disambiguationData":[TD([[makeQuery(id+"F2.imprint","IMPRINT",EDGE,{"disambiguationData":[TD([[subQ3,-1.0]])],"derivedFrom":subQ0}),-1.0]])]});}
            var Q7;
            {var subQ0=sQuery(id+"F2.wireOp",EDGE,"E25");var subQ1=sQuery(id+"F0.wireOp",EDGE,"E17");var subQ2=makeQuery(id+"F1.opExtrude","SWEPT_EDGE",EDGE,{"disambiguationData":[OSD([sQuery(id+"F0.wireOp",EDGE,"E16.0"),subQ1])]});var subQ3=makeQuery(id+"F2.imprint","INTERSECT",VERTEX,{"derivedFrom":[subQ2,subQ0]});Q7=makeQuery(id+"F2.imprint","IMPRINT",FACE,{"disambiguationData":[TD([[makeQuery(id+"F2.imprint","IMPRINT",EDGE,{"disambiguationData":[TD([[subQ3,1.0]])],"derivedFrom":subQ0}),-1.0]])]});}
            extrude(context, id + "F3", {"entities" : qUnion([Q0, Q1, Q2, Q3, Q4, Q5, Q6, Q7]), "operationType" : NewBodyOperationType.ADD, "oppositeDirection" : true, "depth" : 2 * mm});
        }
        {
            var Q0;
            {var subQ0=sQuery(id+"F2.wireOp",EDGE,"E25");var subQ1=sQuery(id+"F0.wireOp",EDGE,"E17");var subQ2=makeQuery(id+"F1.opExtrude","SWEPT_EDGE",EDGE,{"disambiguationData":[OSD([sQuery(id+"F0.wireOp",EDGE,"E16.0"),subQ1])]});var subQ3=makeQuery(id+"F2.imprint","INTERSECT",VERTEX,{"derivedFrom":[subQ2,subQ0]});Q0=makeQuery(id+"F2.imprint","IMPRINT",FACE,{"disambiguationData":[TD([[makeQuery(id+"F2.imprint","IMPRINT",EDGE,{"disambiguationData":[TD([[subQ3,-1.0]])],"derivedFrom":subQ0}),1.0]])]});}
            var Q1;
            {var subQ0=sQuery(id+"F2.wireOp",EDGE,"E25");var subQ1=sQuery(id+"F0.wireOp",EDGE,"E17");var subQ2=makeQuery(id+"F1.opExtrude","SWEPT_EDGE",EDGE,{"disambiguationData":[OSD([sQuery(id+"F0.wireOp",EDGE,"E16.0"),subQ1])]});var subQ3=makeQuery(id+"F2.imprint","INTERSECT",VERTEX,{"derivedFrom":[subQ2,subQ0]});Q1=makeQuery(id+"F2.imprint","IMPRINT",FACE,{"disambiguationData":[TD([[makeQuery(id+"F2.imprint","IMPRINT",EDGE,{"disambiguationData":[TD([[subQ3,1.0]])],"derivedFrom":subQ0}),1.0]])]});}
            var Q2;
            {var subQ0=sQuery(id+"F2.wireOp",EDGE,"E26");var subQ1=sQuery(id+"F0.wireOp",EDGE,"E2");var subQ2=makeQuery(id+"F1.opExtrude","SWEPT_EDGE",EDGE,{"disambiguationData":[OSD([sQuery(id+"F0.wireOp",EDGE,"E1"),subQ1,sQuery(id+"F0.wireOp",EDGE,"E6"),sQuery(id+"F0.wireOp",EDGE,"E20")])]});var subQ3=makeQuery(id+"F2.imprint","INTERSECT",VERTEX,{"derivedFrom":[subQ2,subQ0]});Q2=makeQuery(id+"F2.imprint","IMPRINT",FACE,{"disambiguationData":[TD([[makeQuery(id+"F2.imprint","IMPRINT",EDGE,{"disambiguationData":[TD([[subQ3,1.0]])],"derivedFrom":subQ0}),1.0]])]});}
            var Q3;
            {var subQ0=sQuery(id+"F2.wireOp",EDGE,"E26");var subQ1=sQuery(id+"F0.wireOp",EDGE,"E2");var subQ2=makeQuery(id+"F1.opExtrude","SWEPT_EDGE",EDGE,{"disambiguationData":[OSD([sQuery(id+"F0.wireOp",EDGE,"E1"),subQ1,sQuery(id+"F0.wireOp",EDGE,"E6"),sQuery(id+"F0.wireOp",EDGE,"E20")])]});var subQ3=makeQuery(id+"F2.imprint","INTERSECT",VERTEX,{"derivedFrom":[subQ2,subQ0]});Q3=makeQuery(id+"F2.imprint","IMPRINT",FACE,{"disambiguationData":[TD([[makeQuery(id+"F2.imprint","IMPRINT",EDGE,{"disambiguationData":[TD([[subQ3,-1.0]])],"derivedFrom":subQ0}),1.0]])]});}
            extrude(context, id + "F4", {"entities" : qUnion([Q0, Q1, Q2, Q3]), "operationType" : NewBodyOperationType.ADD, "depth" : 1.5 * mm});
        }
        {
            var Q0;
            Q0=makeQuery(id+"F1.opExtrude","SWEPT_FACE",FACE,{"disambiguationData":[OSD([sQuery(id+"F0.wireOp",EDGE,"E0.right"),sQuery(id+"F0.wireOp",EDGE,"E18")])]});
            var sketch = newSketch(context, id + "F5", { "sketchPlane" : qUnion([Q0])});
            skCircle(sketch, "E29", {"center": v(25, 0) * mm, "radius": 0.8 * mm});
            skCircle(sketch, "E30", {"center": v(-52.5, 0) * mm, "radius": 0.8 * mm});
            skCircle(sketch, "E31", {"center": v(-52.5, 0) * mm, "radius": 2.5 * mm});
            skCircle(sketch, "E32", {"center": v(25, 0) * mm, "radius": 2.5 * mm});
            skSolve(sketch);
        }
        {
            var Q0;
            {var subQ0=sQuery(id+"F5.wireOp",EDGE,"E29");var subQ1=sQuery(id+"F0.wireOp",EDGE,"E0.right");var subQ4=makeQuery(id+"F1.opExtrude","CAP_EDGE",EDGE,{"disambiguationData":[OSD([subQ1,sQuery(id+"F0.wireOp",EDGE,"E18")])],"isStart":true});var subQ5=makeQuery(id+"F5.imprint","INTERSECT",VERTEX,{"derivedFrom":[subQ4,subQ0]});Q0=makeQuery(id+"F5.imprint","IMPRINT",FACE,{"disambiguationData":[TD([[makeQuery(id+"F5.imprint","IMPRINT",EDGE,{"disambiguationData":[TD([[subQ5,1.0]])],"derivedFrom":subQ0}),1.0]])]});}
            var Q1;
            {var subQ0=sQuery(id+"F5.wireOp",EDGE,"E29");var subQ1=sQuery(id+"F0.wireOp",EDGE,"E0.right");var subQ4=makeQuery(id+"F1.opExtrude","CAP_EDGE",EDGE,{"disambiguationData":[OSD([subQ1,sQuery(id+"F0.wireOp",EDGE,"E18")])],"isStart":true});var subQ5=makeQuery(id+"F5.imprint","INTERSECT",VERTEX,{"derivedFrom":[subQ4,subQ0]});Q1=makeQuery(id+"F5.imprint","IMPRINT",FACE,{"disambiguationData":[TD([[makeQuery(id+"F5.imprint","IMPRINT",EDGE,{"disambiguationData":[TD([[subQ5,-1.0]])],"derivedFrom":subQ0}),1.0]])]});}
            var Q2;
            {var subQ0=sQuery(id+"F5.wireOp",EDGE,"E29");var subQ1=sQuery(id+"F0.wireOp",EDGE,"E0.right");var subQ4=sQuery(id+"F0.wireOp",EDGE,"E18");var subQ5=makeQuery(id+"F1.opExtrude","CAP_EDGE",EDGE,{"disambiguationData":[OSD([subQ1,subQ4])],"isStart":true});var subQ6=makeQuery(id+"F5.imprint","INTERSECT",VERTEX,{"derivedFrom":[subQ5,subQ0]});Q2=makeQuery(id+"F5.imprint","IMPRINT",FACE,{"disambiguationData":[TD([[makeQuery(id+"F5.imprint","IMPRINT",EDGE,{"disambiguationData":[TD([[subQ6,1.0]])],"derivedFrom":subQ0}),-1.0]])]});}
            var Q3;
            {var subQ0=sQuery(id+"F5.wireOp",EDGE,"E29");var subQ1=sQuery(id+"F0.wireOp",EDGE,"E0.right");var subQ4=sQuery(id+"F0.wireOp",EDGE,"E18");var subQ5=makeQuery(id+"F1.opExtrude","CAP_EDGE",EDGE,{"disambiguationData":[OSD([subQ1,subQ4])],"isStart":true});var subQ6=makeQuery(id+"F5.imprint","INTERSECT",VERTEX,{"derivedFrom":[subQ5,subQ0]});Q3=makeQuery(id+"F5.imprint","IMPRINT",FACE,{"disambiguationData":[TD([[makeQuery(id+"F5.imprint","IMPRINT",EDGE,{"disambiguationData":[TD([[subQ6,-1.0]])],"derivedFrom":subQ0}),-1.0]])]});}
            var Q4;
            {var subQ0=sQuery(id+"F5.wireOp",EDGE,"E30");var subQ1=sQuery(id+"F0.wireOp",EDGE,"E18");var subQ2=makeQuery(id+"F1.opExtrude","SWEPT_EDGE",EDGE,{"disambiguationData":[OSD([sQuery(id+"F0.wireOp",EDGE,"E15.0"),subQ1])]});var subQ3=makeQuery(id+"F5.imprint","INTERSECT",VERTEX,{"derivedFrom":[subQ2,subQ0]});Q4=makeQuery(id+"F5.imprint","IMPRINT",FACE,{"disambiguationData":[TD([[makeQuery(id+"F5.imprint","IMPRINT",EDGE,{"disambiguationData":[TD([[subQ3,-1.0]])],"derivedFrom":subQ0}),1.0]])]});}
            var Q5;
            {var subQ0=sQuery(id+"F5.wireOp",EDGE,"E30");var subQ1=sQuery(id+"F0.wireOp",EDGE,"E18");var subQ2=makeQuery(id+"F1.opExtrude","SWEPT_EDGE",EDGE,{"disambiguationData":[OSD([sQuery(id+"F0.wireOp",EDGE,"E15.0"),subQ1])]});var subQ3=makeQuery(id+"F5.imprint","INTERSECT",VERTEX,{"derivedFrom":[subQ2,subQ0]});Q5=makeQuery(id+"F5.imprint","IMPRINT",FACE,{"disambiguationData":[TD([[makeQuery(id+"F5.imprint","IMPRINT",EDGE,{"disambiguationData":[TD([[subQ3,1.0]])],"derivedFrom":subQ0}),1.0]])]});}
            var Q6;
            {var subQ0=sQuery(id+"F5.wireOp",EDGE,"E30");var subQ1=sQuery(id+"F0.wireOp",EDGE,"E18");var subQ2=makeQuery(id+"F1.opExtrude","SWEPT_EDGE",EDGE,{"disambiguationData":[OSD([sQuery(id+"F0.wireOp",EDGE,"E15.0"),subQ1])]});var subQ3=makeQuery(id+"F5.imprint","INTERSECT",VERTEX,{"derivedFrom":[subQ2,subQ0]});Q6=makeQuery(id+"F5.imprint","IMPRINT",FACE,{"disambiguationData":[TD([[makeQuery(id+"F5.imprint","IMPRINT",EDGE,{"disambiguationData":[TD([[subQ3,1.0]])],"derivedFrom":subQ0}),-1.0]])]});}
            var Q7;
            {var subQ0=sQuery(id+"F5.wireOp",EDGE,"E30");var subQ1=sQuery(id+"F0.wireOp",EDGE,"E18");var subQ2=makeQuery(id+"F1.opExtrude","SWEPT_EDGE",EDGE,{"disambiguationData":[OSD([sQuery(id+"F0.wireOp",EDGE,"E15.0"),subQ1])]});var subQ3=makeQuery(id+"F5.imprint","INTERSECT",VERTEX,{"derivedFrom":[subQ2,subQ0]});Q7=makeQuery(id+"F5.imprint","IMPRINT",FACE,{"disambiguationData":[TD([[makeQuery(id+"F5.imprint","IMPRINT",EDGE,{"disambiguationData":[TD([[subQ3,-1.0]])],"derivedFrom":subQ0}),-1.0]])]});}
            extrude(context, id + "F6", {"entities" : qUnion([Q0, Q1, Q2, Q3, Q4, Q5, Q6, Q7]), "operationType" : NewBodyOperationType.ADD, "oppositeDirection" : true, "depth" : 2 * mm});
        }
        {
            var Q0;
            {var subQ0=sQuery(id+"F5.wireOp",EDGE,"E30");var subQ1=sQuery(id+"F0.wireOp",EDGE,"E18");var subQ2=makeQuery(id+"F1.opExtrude","SWEPT_EDGE",EDGE,{"disambiguationData":[OSD([sQuery(id+"F0.wireOp",EDGE,"E15.0"),subQ1])]});var subQ3=makeQuery(id+"F5.imprint","INTERSECT",VERTEX,{"derivedFrom":[subQ2,subQ0]});Q0=makeQuery(id+"F5.imprint","IMPRINT",FACE,{"disambiguationData":[TD([[makeQuery(id+"F5.imprint","IMPRINT",EDGE,{"disambiguationData":[TD([[subQ3,1.0]])],"derivedFrom":subQ0}),1.0]])]});}
            var Q1;
            {var subQ0=sQuery(id+"F5.wireOp",EDGE,"E30");var subQ1=sQuery(id+"F0.wireOp",EDGE,"E18");var subQ2=makeQuery(id+"F1.opExtrude","SWEPT_EDGE",EDGE,{"disambiguationData":[OSD([sQuery(id+"F0.wireOp",EDGE,"E15.0"),subQ1])]});var subQ3=makeQuery(id+"F5.imprint","INTERSECT",VERTEX,{"derivedFrom":[subQ2,subQ0]});Q1=makeQuery(id+"F5.imprint","IMPRINT",FACE,{"disambiguationData":[TD([[makeQuery(id+"F5.imprint","IMPRINT",EDGE,{"disambiguationData":[TD([[subQ3,-1.0]])],"derivedFrom":subQ0}),1.0]])]});}
            var Q2;
            {var subQ0=sQuery(id+"F5.wireOp",EDGE,"E29");var subQ1=sQuery(id+"F0.wireOp",EDGE,"E0.right");var subQ4=makeQuery(id+"F1.opExtrude","CAP_EDGE",EDGE,{"disambiguationData":[OSD([subQ1,sQuery(id+"F0.wireOp",EDGE,"E18")])],"isStart":true});var subQ5=makeQuery(id+"F5.imprint","INTERSECT",VERTEX,{"derivedFrom":[subQ4,subQ0]});Q2=makeQuery(id+"F5.imprint","IMPRINT",FACE,{"disambiguationData":[TD([[makeQuery(id+"F5.imprint","IMPRINT",EDGE,{"disambiguationData":[TD([[subQ5,1.0]])],"derivedFrom":subQ0}),1.0]])]});}
            var Q3;
            {var subQ0=sQuery(id+"F5.wireOp",EDGE,"E29");var subQ1=sQuery(id+"F0.wireOp",EDGE,"E0.right");var subQ4=makeQuery(id+"F1.opExtrude","CAP_EDGE",EDGE,{"disambiguationData":[OSD([subQ1,sQuery(id+"F0.wireOp",EDGE,"E18")])],"isStart":true});var subQ5=makeQuery(id+"F5.imprint","INTERSECT",VERTEX,{"derivedFrom":[subQ4,subQ0]});Q3=makeQuery(id+"F5.imprint","IMPRINT",FACE,{"disambiguationData":[TD([[makeQuery(id+"F5.imprint","IMPRINT",EDGE,{"disambiguationData":[TD([[subQ5,-1.0]])],"derivedFrom":subQ0}),1.0]])]});}
            extrude(context, id + "F7", {"entities" : qUnion([Q0, Q1, Q2, Q3]), "operationType" : NewBodyOperationType.ADD, "depth" : 1.5 * mm});
        }
        {
            var Q0;
            Q0=makeQuery(id+"F1.opExtrude","SWEPT_BODY",BODY,{"disambiguationData":[OSD([sQuery(id+"F0.wireOp",EDGE,"E0.right"),sQuery(id+"F0.wireOp",EDGE,"E2"),sQuery(id+"F0.wireOp",EDGE,"E3"),sQuery(id+"F0.wireOp",EDGE,"E4"),sQuery(id+"F0.wireOp",EDGE,"E5"),sQuery(id+"F0.wireOp",EDGE,"E6"),sQuery(id+"F0.wireOp",EDGE,"E7"),sQuery(id+"F0.wireOp",EDGE,"E8"),sQuery(id+"F0.wireOp",EDGE,"E9"),sQuery(id+"F0.wireOp",EDGE,"E10"),sQuery(id+"F0.wireOp",EDGE,"E11.0"),sQuery(id+"F0.wireOp",EDGE,"E12.0"),sQuery(id+"F0.wireOp",EDGE,"E13.0"),sQuery(id+"F0.wireOp",EDGE,"E14.0"),sQuery(id+"F0.wireOp",EDGE,"E15.0"),sQuery(id+"F0.wireOp",EDGE,"E16.0"),sQuery(id+"F0.wireOp",EDGE,"E17"),sQuery(id+"F0.wireOp",EDGE,"E18"),sQuery(id+"F0.wireOp",EDGE,"E19"),sQuery(id+"F0.wireOp",EDGE,"E22"),sQuery(id+"F0.wireOp",EDGE,"E23"),sQuery(id+"F0.wireOp",EDGE,"E24")])]});
            var Q1;
            Q1=makeQuery(id+"F1.opExtrude","CAP_VERTEX",VERTEX,{"disambiguationData":[OSD([sQuery(id+"F0.wireOp",EDGE,"E7"),sQuery(id+"F0.wireOp",EDGE,"E14.0")])],"isStart":false});
            transform(context, id + "F8", {"entities" : qUnion([Q0]), "transformType" : TransformType.SCALE_UNIFORMLY, "scale" : 0.75, "scalePoint" : qUnion([Q1]), "makeCopy" : false});
        }
    });
